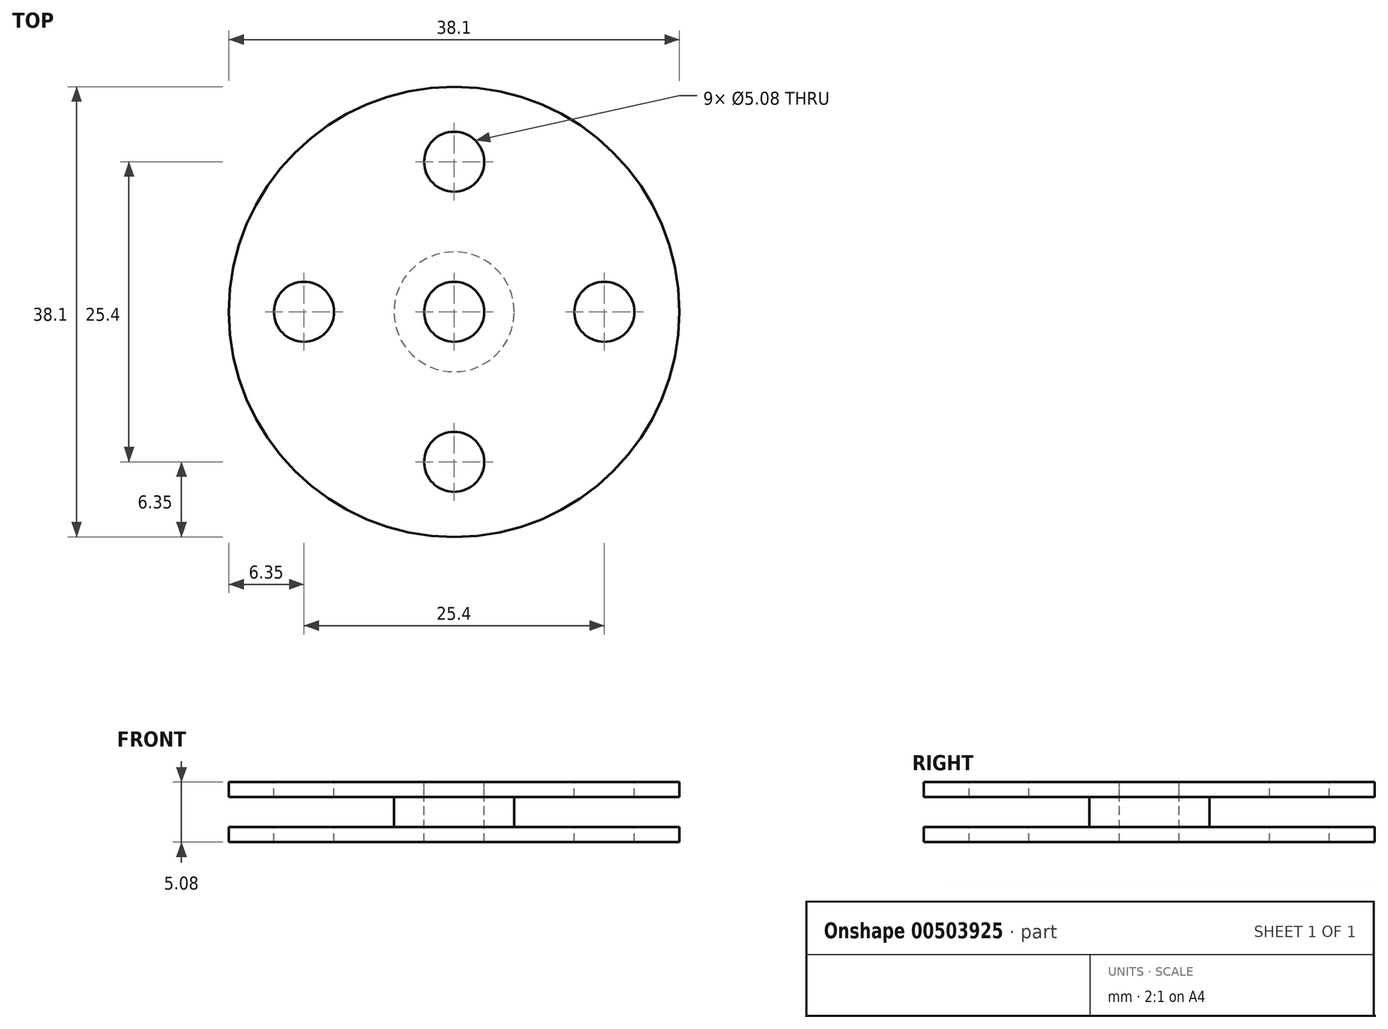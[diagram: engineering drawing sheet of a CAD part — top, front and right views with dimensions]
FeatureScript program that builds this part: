
annotation { "Feature Type Name" : "Feature", "Feature Type Description" : "" }
export const myFeature = defineFeature(function(context is Context, id is Id, definition is map)
    precondition{}
    {
        {
            var Q0;
            Q0=qCreatedBy(makeId("Top.planeOp"),FACE);
            var sketch = newSketch(context, id + "F0", { "sketchPlane" : qUnion([Q0])});
            skCircle(sketch, "E0", {"center": v(0, 0) * mm, "radius": 19.05 * mm});
            skSolve(sketch);
        }
        {
            var Q0;
            Q0=makeQuery(id+"F0.imprint","IMPRINT",FACE,{"disambiguationData":[TD([[makeQuery(id+"F0.imprint","IMPRINT",EDGE,{"derivedFrom":sQuery(id+"F0.wireOp",EDGE,"E0")}),1.0]])]});
            extrude(context, id + "F1", {"entities" : qUnion([Q0]), "depth" : 1.27 * mm});
        }
        {
            var Q0;
            Q0=makeQuery(id+"F1.opExtrude","CAP_FACE",FACE,{"disambiguationData":[OSD([sQuery(id+"F0.wireOp",EDGE,"E0")])],"isStart":false});
            var sketch = newSketch(context, id + "F2", { "sketchPlane" : qUnion([Q0])});
            skCircle(sketch, "E1", {"center": v(0, 0) * mm, "radius": 5.08 * mm});
            skSolve(sketch);
        }
        {
            var Q0;
            Q0=makeQuery(id+"F2.imprint","IMPRINT",FACE,{"disambiguationData":[TD([[makeQuery(id+"F2.imprint","IMPRINT",EDGE,{"derivedFrom":sQuery(id+"F2.wireOp",EDGE,"E1")}),1.0]])]});
            extrude(context, id + "F3", {"entities" : qUnion([Q0]), "operationType" : NewBodyOperationType.ADD, "depth" : 2.54 * mm});
        }
        {
            var Q0;
            Q0=makeQuery(id+"F3.opExtrude","CAP_FACE",FACE,{"disambiguationData":[OSD([sQuery(id+"F2.wireOp",EDGE,"E1")])],"isStart":false});
            var sketch = newSketch(context, id + "F4", { "sketchPlane" : qUnion([Q0])});
            skCircle(sketch, "E2", {"center": v(0, 0) * mm, "radius": 19.05 * mm});
            skSolve(sketch);
        }
        {
            var Q0;
            Q0=makeQuery(id+"F4.imprint","IMPRINT",FACE,{"disambiguationData":[TD([[makeQuery(id+"F4.imprint","IMPRINT",EDGE,{"derivedFrom":makeQuery(id+"F3.opExtrude","CAP_EDGE",EDGE,{"disambiguationData":[OSD([sQuery(id+"F2.wireOp",EDGE,"E1")])],"isStart":false})}),1.0]])]});
            var Q1;
            Q1=makeQuery(id+"F4.imprint","IMPRINT",FACE,{"disambiguationData":[TD([[makeQuery(id+"F4.imprint","IMPRINT",EDGE,{"derivedFrom":sQuery(id+"F4.wireOp",EDGE,"E2")}),1.0]])]});
            extrude(context, id + "F5", {"entities" : qUnion([Q0, Q1]), "operationType" : NewBodyOperationType.ADD, "depth" : 1.27 * mm});
        }
        {
            var Q0;
            Q0=makeQuery(id+"F5.opExtrude","CAP_FACE",FACE,{"disambiguationData":[OSD([sQuery(id+"F4.wireOp",EDGE,"E2")])],"isStart":false});
            var sketch = newSketch(context, id + "F6", { "sketchPlane" : qUnion([Q0])});
            skCircle(sketch, "E3", {"center": v(0, 0) * mm, "radius": 2.54 * mm});
            skSolve(sketch);
        }
        {
            var Q0;
            Q0=makeQuery(id+"F6.imprint","IMPRINT",FACE,{"disambiguationData":[TD([[makeQuery(id+"F6.imprint","IMPRINT",EDGE,{"derivedFrom":sQuery(id+"F6.wireOp",EDGE,"E3")}),1.0]])]});
            extrude(context, id + "F7", {"entities" : qUnion([Q0]), "operationType" : NewBodyOperationType.REMOVE, "oppositeDirection" : true, "depth" : 25.4 * mm});
        }
        {
            var Q0;
            Q0=makeQuery(id+"F5.opExtrude","CAP_FACE",FACE,{"disambiguationData":[OSD([sQuery(id+"F4.wireOp",EDGE,"E2")])],"isStart":false});
            var sketch = newSketch(context, id + "F8", { "sketchPlane" : qUnion([Q0])});
            skCircle(sketch, "E4", {"center": v(0, 12.7) * mm, "radius": 2.54 * mm});
            skLineSegment(sketch, "E5", {"start": v(0, 12.7) * mm, "end": v(0, 0) * mm});
            skLineSegment(sketch, "E6", {"start": v(0, 0) * mm, "end": v(12.7, 0) * mm});
            skLineSegment(sketch, "E7", {"start": v(0, 0) * mm, "end": v(0, -12.7) * mm});
            skLineSegment(sketch, "E8", {"start": v(0, 0) * mm, "end": v(-12.7, 0) * mm});
            skCircle(sketch, "E9", {"center": v(12.7, 0) * mm, "radius": 2.54 * mm});
            skCircle(sketch, "E10", {"center": v(0, -12.7) * mm, "radius": 2.54 * mm});
            skCircle(sketch, "E11", {"center": v(-12.7, 0) * mm, "radius": 2.54 * mm});
            skSolve(sketch);
        }
        {
            var Q0;
            Q0=makeQuery(id+"F8.imprint","IMPRINT",FACE,{"disambiguationData":[TD([[makeQuery(id+"F8.imprint","IMPRINT",EDGE,{"derivedFrom":sQuery(id+"F8.wireOp",EDGE,"E4")}),1.0]])]});
            var Q1;
            Q1=makeQuery(id+"F8.imprint","IMPRINT",FACE,{"disambiguationData":[TD([[makeQuery(id+"F8.imprint","IMPRINT",EDGE,{"derivedFrom":sQuery(id+"F8.wireOp",EDGE,"E9")}),1.0]])]});
            var Q2;
            Q2=makeQuery(id+"F8.imprint","IMPRINT",FACE,{"disambiguationData":[TD([[makeQuery(id+"F8.imprint","IMPRINT",EDGE,{"derivedFrom":sQuery(id+"F8.wireOp",EDGE,"E10")}),1.0]])]});
            var Q3;
            Q3=makeQuery(id+"F8.imprint","IMPRINT",FACE,{"disambiguationData":[TD([[makeQuery(id+"F8.imprint","IMPRINT",EDGE,{"derivedFrom":sQuery(id+"F8.wireOp",EDGE,"E11")}),1.0]])]});
            extrude(context, id + "F9", {"entities" : qUnion([Q0, Q1, Q2, Q3]), "operationType" : NewBodyOperationType.REMOVE, "oppositeDirection" : true, "depth" : 25.4 * mm});
        }
    });
